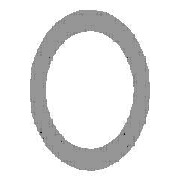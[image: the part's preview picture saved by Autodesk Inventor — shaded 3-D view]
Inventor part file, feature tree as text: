
AUTODESK INVENTOR PART (.ipt)
format: ipt  version: 2013 (Build 170138000, 138)  size: 109,056 bytes
history: native  units: mm (DEFAULTED — no unit token found)
features: other x4, sketch x3, plane x1
ambient origin geometry x8: Origin, YZ Plane, XZ Plane, XY Plane, X Axis, Y Axis, Z Axis, Center Point
bodies: Solid1 (feature_tree), Body (feature_tree)
feature tree (8):
  parser-record x1  (decoder bookkeeping rows leaked as tree rows — omitted from the tree; the rows remain in map.json)
  other  "Driven Length"
  other  "Start plane"
  other  "End plane"
  sketch  "Sketch"  dims[d2=365.252mm d3=0.0mm d4=-0.0mm d5=365.252mm d6=90.0deg d7=365.252mm]
  sketch  "Sketch3"  dims[d0=42.164mm]
  plane  "Work Plane3"
  sketch  "Sketch4"  dims[d1=3.556mm]
